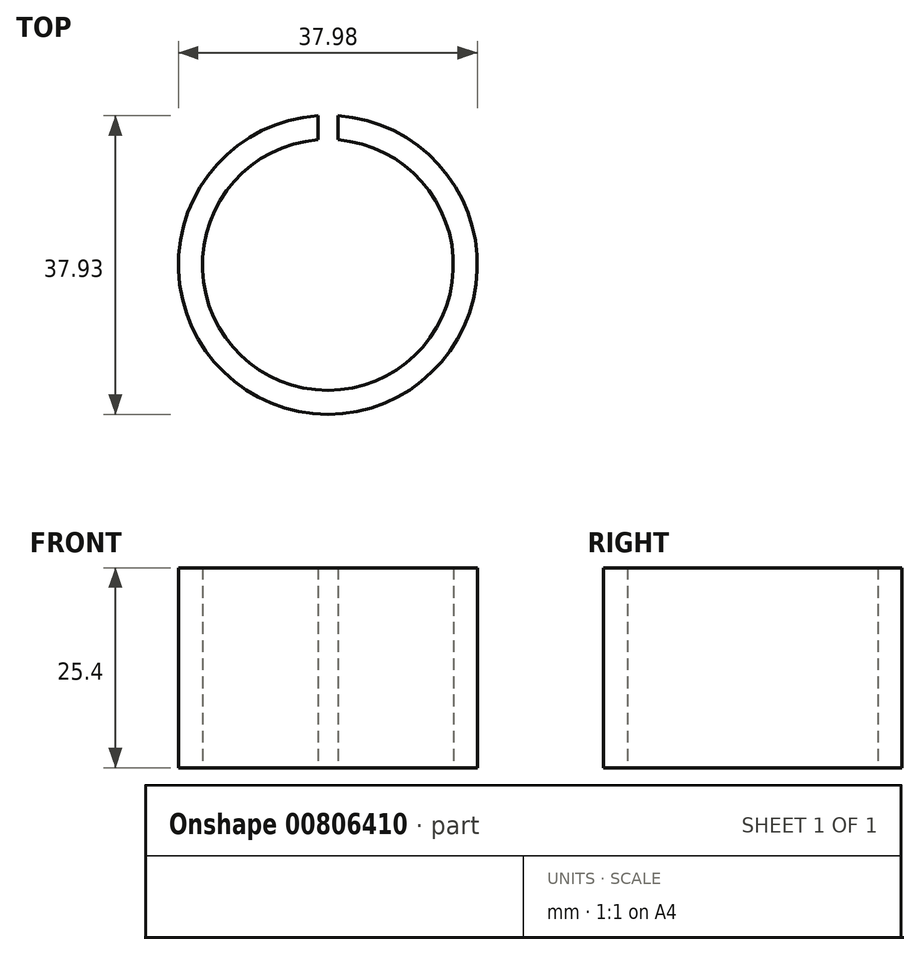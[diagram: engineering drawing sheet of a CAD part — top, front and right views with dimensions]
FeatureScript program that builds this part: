
annotation { "Feature Type Name" : "Feature", "Feature Type Description" : "" }
export const myFeature = defineFeature(function(context is Context, id is Id, definition is map)
    precondition{}
    {
        {
            var Q0;
            Q0=qCreatedBy(makeId("Top.planeOp"),FACE);
            var sketch = newSketch(context, id + "F0", { "sketchPlane" : qUnion([Q0])});
            skArc(sketch, "E0", {"start": v(-1.27, 15.89) * mm, "mid": v(0, -15.94) * mm, "end": v(1.27, 15.89) * mm});
            skArc(sketch, "E1", {"start": v(-1.27, 18.94) * mm, "mid": v(0, -18.99) * mm, "end": v(1.27, 18.94) * mm});
            skLineSegment(sketch, "E2.left", {"start": v(-1.27, 18.94) * mm, "end": v(-1.27, 15.89) * mm});
            skLineSegment(sketch, "E2.right", {"start": v(1.27, 18.94) * mm, "end": v(1.27, 15.89) * mm});
            skPoint(sketch, "E3.orphan", {"position": v(1.27, 20.62) * mm});
            skPoint(sketch, "E4.orphan", {"position": v(-1.27, 20.62) * mm});
            skPoint(sketch, "E5.orphan", {"position": v(1.27, 0) * mm});
            skSolve(sketch);
        }
        {
            var Q0;
            Q0 = qSketchRegion(id + "F0", true);
            extrude(context, id + "F1", {"entities" : qUnion([Q0]), "depth" : 25.4 * mm, "offsetDistance" : 25.4 * mm});
        }
    });
